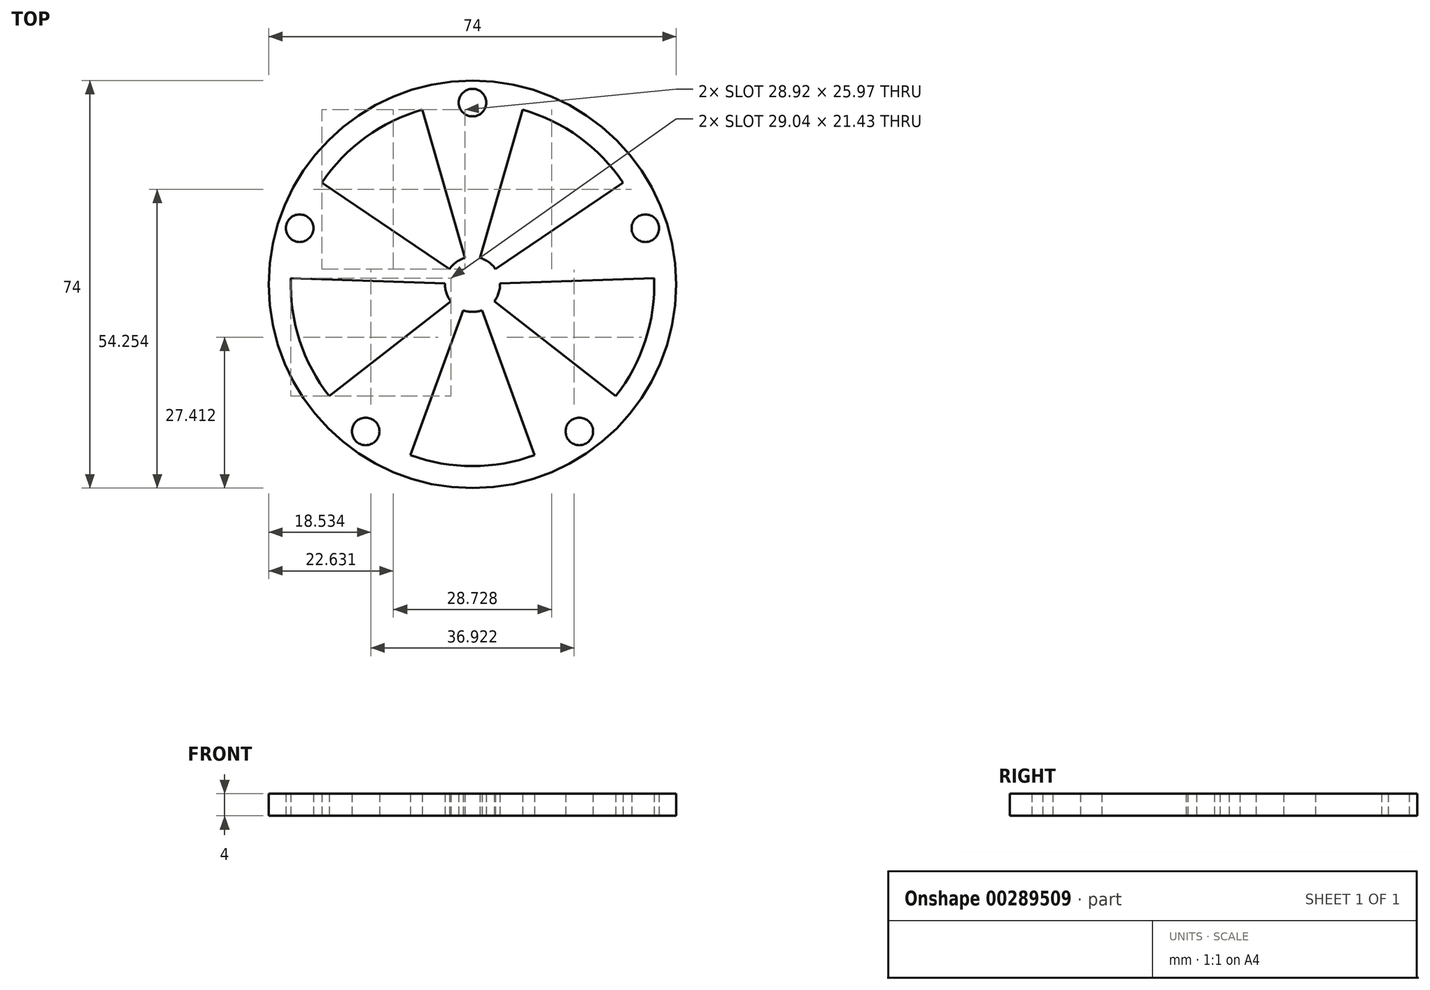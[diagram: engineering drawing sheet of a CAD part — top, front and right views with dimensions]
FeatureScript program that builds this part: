
annotation { "Feature Type Name" : "Feature", "Feature Type Description" : "" }
export const myFeature = defineFeature(function(context is Context, id is Id, definition is map)
    precondition{}
    {
        {
            var Q0;
            Q0=qCreatedBy(makeId("Top.planeOp"),FACE);
            var sketch = newSketch(context, id + "F0", { "sketchPlane" : qUnion([Q0])});
            skCircle(sketch, "E0", {"center": v(-0.61, 12.64) * mm, "radius": 2.5 * mm});
            skCircle(sketch, "E1.1.0", {"center": v(-32, -10.17) * mm, "radius": 2.5 * mm});
            skCircle(sketch, "E1.2.0", {"center": v(-20.01, -47.06) * mm, "radius": 2.5 * mm});
            skCircle(sketch, "E1.3.0", {"center": v(18.78, -47.06) * mm, "radius": 2.5 * mm});
            skCircle(sketch, "E1.4.0", {"center": v(30.77, -10.17) * mm, "radius": 2.5 * mm});
            skPoint(sketch, "E1.center", {"position": v(-0.61, -20.36) * mm});
            skLineSegment(sketch, "E2", {"start": v(22.92, -4.47) * mm, "end": v(-0.61, -20.36) * mm});
            skLineSegment(sketch, "E3", {"start": v(22.92, -4.47) * mm, "end": v(26.73, -1.9) * mm});
            skLineSegment(sketch, "E4", {"start": v(7.23, 6.94) * mm, "end": v(-0.61, -20.36) * mm});
            skLineSegment(sketch, "E5", {"start": v(-0.61, -20.36) * mm, "end": v(8.5, 11.35) * mm});
            skLineSegment(sketch, "E6.1.0", {"start": v(-0.61, -20.36) * mm, "end": v(-27.96, -1.9) * mm});
            skLineSegment(sketch, "E6.1.2", {"start": v(-8.46, 6.94) * mm, "end": v(-0.61, -20.36) * mm});
            skLineSegment(sketch, "E6.1.4", {"start": v(-8.46, 6.94) * mm, "end": v(-9.73, 11.35) * mm});
            skLineSegment(sketch, "E6.2.0", {"start": v(-0.61, -20.36) * mm, "end": v(-26.63, -40.66) * mm});
            skLineSegment(sketch, "E6.2.2", {"start": v(-29, -19.39) * mm, "end": v(-0.61, -20.36) * mm});
            skLineSegment(sketch, "E6.2.4", {"start": v(-29, -19.39) * mm, "end": v(-33.6, -19.23) * mm});
            skLineSegment(sketch, "E6.3.0", {"start": v(-0.61, -20.36) * mm, "end": v(10.65, -51.38) * mm});
            skLineSegment(sketch, "E6.3.2", {"start": v(-10.31, -47.06) * mm, "end": v(-0.61, -20.36) * mm});
            skLineSegment(sketch, "E6.3.4", {"start": v(-10.31, -47.06) * mm, "end": v(-11.88, -51.38) * mm});
            skLineSegment(sketch, "E6.4.0", {"start": v(-0.61, -20.36) * mm, "end": v(32.37, -19.23) * mm});
            skLineSegment(sketch, "E6.4.2", {"start": v(21.78, -37.84) * mm, "end": v(-0.61, -20.36) * mm});
            skLineSegment(sketch, "E6.4.4", {"start": v(21.78, -37.84) * mm, "end": v(25.4, -40.66) * mm});
            skCircle(sketch, "E7", {"center": v(-0.61, -20.36) * mm, "radius": 37 * mm});
            skCircle(sketch, "E8", {"center": v(-0.61, -20.36) * mm, "radius": 33 * mm});
            skCircle(sketch, "E9", {"center": v(-0.61, -20.36) * mm, "radius": 5 * mm});
            skSolve(sketch);
        }
        {
            var Q0;
            Q0 = qSketchRegion(id + "F0", true);
            var Q1;
            {var subQ1=sQuery(id+"F0.wireOp",EDGE,"E2");var subQ3=sQuery(id+"F0.wireOp",EDGE,"E9");var subQ4=makeQuery(id+"F0.imprint","INTERSECT",VERTEX,{"derivedFrom":[subQ1,subQ3]});Q1=makeQuery(id+"F0.imprint","IMPRINT",FACE,{"disambiguationData":[TD([[makeQuery(id+"F0.imprint","IMPRINT",EDGE,{"disambiguationData":[TD([[subQ4,-1.0]])],"derivedFrom":subQ3}),1.0]])]});}
            var Q2;
            {var subQ1=sQuery(id+"F0.wireOp",EDGE,"E5");var subQ3=sQuery(id+"F0.wireOp",EDGE,"E9");var subQ4=makeQuery(id+"F0.imprint","INTERSECT",VERTEX,{"derivedFrom":[subQ1,subQ3]});Q2=makeQuery(id+"F0.imprint","IMPRINT",FACE,{"disambiguationData":[TD([[makeQuery(id+"F0.imprint","IMPRINT",EDGE,{"disambiguationData":[TD([[subQ4,-1.0]])],"derivedFrom":subQ3}),1.0]])]});}
            var Q3;
            {var subQ1=sQuery(id+"F0.wireOp",EDGE,"E6.1.0");var subQ3=sQuery(id+"F0.wireOp",EDGE,"E9");var subQ4=makeQuery(id+"F0.imprint","INTERSECT",VERTEX,{"derivedFrom":[subQ1,subQ3]});Q3=makeQuery(id+"F0.imprint","IMPRINT",FACE,{"disambiguationData":[TD([[makeQuery(id+"F0.imprint","IMPRINT",EDGE,{"disambiguationData":[TD([[subQ4,1.0]])],"derivedFrom":subQ3}),1.0]])]});}
            var Q4;
            {var subQ1=sQuery(id+"F0.wireOp",EDGE,"E6.1.0");var subQ3=sQuery(id+"F0.wireOp",EDGE,"E9");var subQ4=makeQuery(id+"F0.imprint","INTERSECT",VERTEX,{"derivedFrom":[subQ1,subQ3]});Q4=makeQuery(id+"F0.imprint","IMPRINT",FACE,{"disambiguationData":[TD([[makeQuery(id+"F0.imprint","IMPRINT",EDGE,{"disambiguationData":[TD([[subQ4,-1.0]])],"derivedFrom":subQ3}),1.0]])]});}
            var Q5;
            {var subQ1=sQuery(id+"F0.wireOp",EDGE,"E6.2.0");var subQ3=sQuery(id+"F0.wireOp",EDGE,"E9");var subQ4=makeQuery(id+"F0.imprint","INTERSECT",VERTEX,{"derivedFrom":[subQ1,subQ3]});Q5=makeQuery(id+"F0.imprint","IMPRINT",FACE,{"disambiguationData":[TD([[makeQuery(id+"F0.imprint","IMPRINT",EDGE,{"disambiguationData":[TD([[subQ4,1.0]])],"derivedFrom":subQ3}),1.0]])]});}
            var Q6;
            {var subQ1=sQuery(id+"F0.wireOp",EDGE,"E6.2.0");var subQ3=sQuery(id+"F0.wireOp",EDGE,"E9");var subQ4=makeQuery(id+"F0.imprint","INTERSECT",VERTEX,{"derivedFrom":[subQ1,subQ3]});Q6=makeQuery(id+"F0.imprint","IMPRINT",FACE,{"disambiguationData":[TD([[makeQuery(id+"F0.imprint","IMPRINT",EDGE,{"disambiguationData":[TD([[subQ4,-1.0]])],"derivedFrom":subQ3}),1.0]])]});}
            var Q7;
            {var subQ1=sQuery(id+"F0.wireOp",EDGE,"E6.3.0");var subQ3=sQuery(id+"F0.wireOp",EDGE,"E9");var subQ4=makeQuery(id+"F0.imprint","INTERSECT",VERTEX,{"derivedFrom":[subQ1,subQ3]});Q7=makeQuery(id+"F0.imprint","IMPRINT",FACE,{"disambiguationData":[TD([[makeQuery(id+"F0.imprint","IMPRINT",EDGE,{"disambiguationData":[TD([[subQ4,1.0]])],"derivedFrom":subQ3}),1.0]])]});}
            var Q8;
            {var subQ1=sQuery(id+"F0.wireOp",EDGE,"E6.3.0");var subQ3=sQuery(id+"F0.wireOp",EDGE,"E9");var subQ4=makeQuery(id+"F0.imprint","INTERSECT",VERTEX,{"derivedFrom":[subQ1,subQ3]});Q8=makeQuery(id+"F0.imprint","IMPRINT",FACE,{"disambiguationData":[TD([[makeQuery(id+"F0.imprint","IMPRINT",EDGE,{"disambiguationData":[TD([[subQ4,-1.0]])],"derivedFrom":subQ3}),1.0]])]});}
            var Q9;
            {var subQ1=sQuery(id+"F0.wireOp",EDGE,"E2");var subQ3=sQuery(id+"F0.wireOp",EDGE,"E9");var subQ4=makeQuery(id+"F0.imprint","INTERSECT",VERTEX,{"derivedFrom":[subQ1,subQ3]});Q9=makeQuery(id+"F0.imprint","IMPRINT",FACE,{"disambiguationData":[TD([[makeQuery(id+"F0.imprint","IMPRINT",EDGE,{"disambiguationData":[TD([[subQ4,1.0]])],"derivedFrom":subQ3}),1.0]])]});}
            var Q10;
            {var subQ1=sQuery(id+"F0.wireOp",EDGE,"E6.4.0");var subQ3=sQuery(id+"F0.wireOp",EDGE,"E9");var subQ4=makeQuery(id+"F0.imprint","INTERSECT",VERTEX,{"derivedFrom":[subQ1,subQ3]});Q10=makeQuery(id+"F0.imprint","IMPRINT",FACE,{"disambiguationData":[TD([[makeQuery(id+"F0.imprint","IMPRINT",EDGE,{"disambiguationData":[TD([[subQ4,1.0]])],"derivedFrom":subQ3}),1.0]])]});}
            var Q11;
            {var subQ0=sQuery(id+"F0.wireOp",EDGE,"E6.1.4");Q11=makeQuery(id+"F0.imprint","IMPRINT",FACE,{"disambiguationData":[TD([[makeQuery(id+"F0.imprint","IMPRINT",EDGE,{"derivedFrom":subQ0}),-1.0]])]});}
            var Q12;
            {var subQ5=sQuery(id+"F0.wireOp",EDGE,"E3");Q12=makeQuery(id+"F0.imprint","IMPRINT",FACE,{"disambiguationData":[TD([[makeQuery(id+"F0.imprint","IMPRINT",EDGE,{"derivedFrom":subQ5}),-1.0]])]});}
            var Q13;
            {var subQ0=sQuery(id+"F0.wireOp",EDGE,"E6.4.4");Q13=makeQuery(id+"F0.imprint","IMPRINT",FACE,{"disambiguationData":[TD([[makeQuery(id+"F0.imprint","IMPRINT",EDGE,{"derivedFrom":subQ0}),-1.0]])]});}
            var Q14;
            {var subQ0=sQuery(id+"F0.wireOp",EDGE,"E6.3.4");Q14=makeQuery(id+"F0.imprint","IMPRINT",FACE,{"disambiguationData":[TD([[makeQuery(id+"F0.imprint","IMPRINT",EDGE,{"derivedFrom":subQ0}),-1.0]])]});}
            var Q15;
            {var subQ0=sQuery(id+"F0.wireOp",EDGE,"E6.2.4");Q15=makeQuery(id+"F0.imprint","IMPRINT",FACE,{"disambiguationData":[TD([[makeQuery(id+"F0.imprint","IMPRINT",EDGE,{"derivedFrom":subQ0}),-1.0]])]});}
            extrude(context, id + "F1", {"entities" : qUnion([Q0, Q1, Q2, Q3, Q4, Q5, Q6, Q7, Q8, Q9, Q10, Q11, Q12, Q13, Q14, Q15]), "depth" : 4 * mm});
        }
    });
